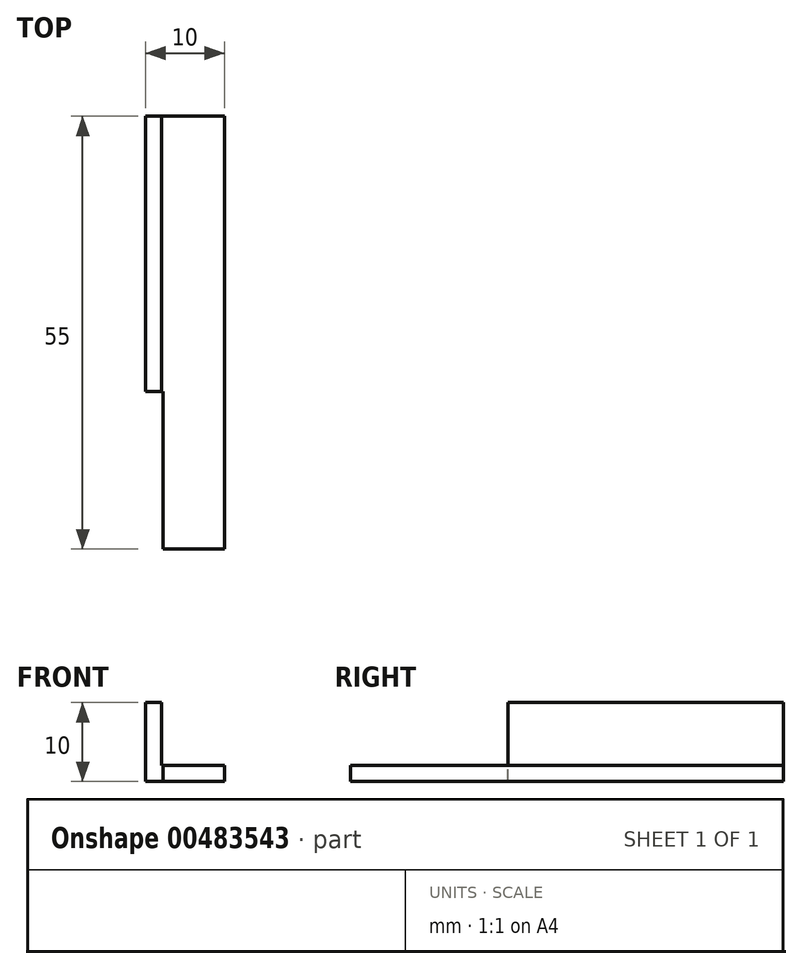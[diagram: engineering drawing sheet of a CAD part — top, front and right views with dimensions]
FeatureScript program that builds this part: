
annotation { "Feature Type Name" : "Feature", "Feature Type Description" : "" }
export const myFeature = defineFeature(function(context is Context, id is Id, definition is map)
    precondition{}
    {
        {
            var Q0;
            Q0=qCreatedBy(makeId("Front.planeOp"),FACE);
            var sketch = newSketch(context, id + "F0", { "sketchPlane" : qUnion([Q0])});
            skLineSegment(sketch, "E0", {"start": v(0, 0) * mm, "end": v(10, 0) * mm});
            skLineSegment(sketch, "E1", {"start": v(10, 0) * mm, "end": v(10, 2) * mm});
            skLineSegment(sketch, "E2", {"start": v(10, 2) * mm, "end": v(2, 2) * mm});
            skLineSegment(sketch, "E3", {"start": v(2, 2) * mm, "end": v(2, 10) * mm});
            skLineSegment(sketch, "E4", {"start": v(2, 10) * mm, "end": v(0, 10) * mm});
            skLineSegment(sketch, "E5", {"start": v(0, 10) * mm, "end": v(0, 0) * mm});
            skSolve(sketch);
        }
        {
            var Q0;
            Q0 = qSketchRegion(id + "F0", true);
            extrude(context, id + "F1", {"entities" : qUnion([Q0]), "depth" : 55 * mm, "offsetDistance" : 25 * mm});
        }
        {
            var Q0;
            Q0=makeQuery(id+"F1.opExtrude","SWEPT_FACE",FACE,{"disambiguationData":[OSD([sQuery(id+"F0.wireOp",EDGE,"E5")])]});
            var sketch = newSketch(context, id + "F2", { "sketchPlane" : qUnion([Q0])});
            skLineSegment(sketch, "E6.bottom", {"start": v(55, 0) * mm, "end": v(35, 0) * mm});
            skLineSegment(sketch, "E6.top", {"start": v(55, 10) * mm, "end": v(35, 10) * mm});
            skLineSegment(sketch, "E6.left", {"start": v(55, 0) * mm, "end": v(55, 10) * mm});
            skLineSegment(sketch, "E6.right", {"start": v(35, 0) * mm, "end": v(35, 10) * mm});
            skSolve(sketch);
        }
        {
            var Q0;
            Q0 = qSketchRegion(id + "F2", true);
            extrude(context, id + "F3", {"entities" : qUnion([Q0]), "operationType" : NewBodyOperationType.REMOVE, "oppositeDirection" : true, "depth" : 2.2 * mm, "offsetDistance" : 25 * mm});
        }
    });
